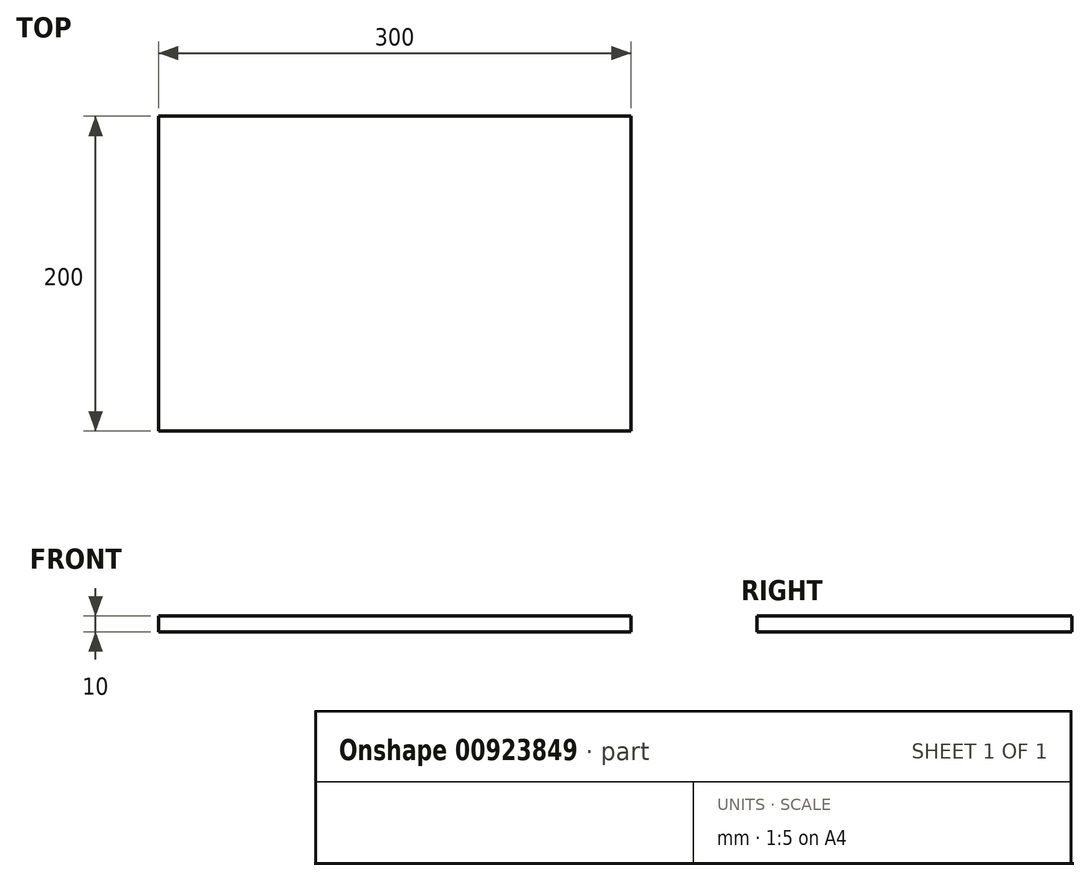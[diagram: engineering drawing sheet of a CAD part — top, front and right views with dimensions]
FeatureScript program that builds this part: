
annotation { "Feature Type Name" : "Feature", "Feature Type Description" : "" }
export const myFeature = defineFeature(function(context is Context, id is Id, definition is map)
    precondition{}
    {
        {
            var Q0;
            Q0=qCreatedBy(makeId("Top.planeOp"),FACE);
            var sketch = newSketch(context, id + "F0", { "sketchPlane" : qUnion([Q0])});
            skLineSegment(sketch, "E0.bottom", {"start": v(150, 100) * mm, "end": v(-150, 100) * mm});
            skLineSegment(sketch, "E0.top", {"start": v(150, -100) * mm, "end": v(-150, -100) * mm});
            skLineSegment(sketch, "E0.left", {"start": v(150, 100) * mm, "end": v(150, -100) * mm});
            skLineSegment(sketch, "E0.right", {"start": v(-150, 100) * mm, "end": v(-150, -100) * mm});
            skPoint(sketch, "E0.middle", {"position": v(0, 0) * mm});
            skLineSegment(sketch, "E1.bottom", {"start": v(115, 80) * mm, "end": v(-115, 80) * mm});
            skLineSegment(sketch, "E1.top", {"start": v(115, -80) * mm, "end": v(-115, -80) * mm});
            skLineSegment(sketch, "E1.left", {"start": v(115, 80) * mm, "end": v(115, -80) * mm});
            skLineSegment(sketch, "E1.right", {"start": v(-115, 80) * mm, "end": v(-115, -80) * mm});
            skPoint(sketch, "E2", {"position": v(-115, 0) * mm});
            skSolve(sketch);
        }
        {
            var Q0;
            Q0=makeQuery(id+"F0.imprint","IMPRINT",FACE,{"disambiguationData":[TD([[makeQuery(id+"F0.imprint","IMPRINT",EDGE,{"derivedFrom":sQuery(id+"F0.wireOp",EDGE,"E0.bottom")}),1.0]])]});
            var Q1;
            Q1=makeQuery(id+"F0.imprint","IMPRINT",FACE,{"disambiguationData":[TD([[makeQuery(id+"F0.imprint","IMPRINT",EDGE,{"derivedFrom":sQuery(id+"F0.wireOp",EDGE,"E1.bottom")}),1.0]])]});
            extrude(context, id + "F1", {"entities" : qUnion([Q0, Q1]), "depth" : 10 * mm, "offsetDistance" : 25 * mm});
        }
    });
